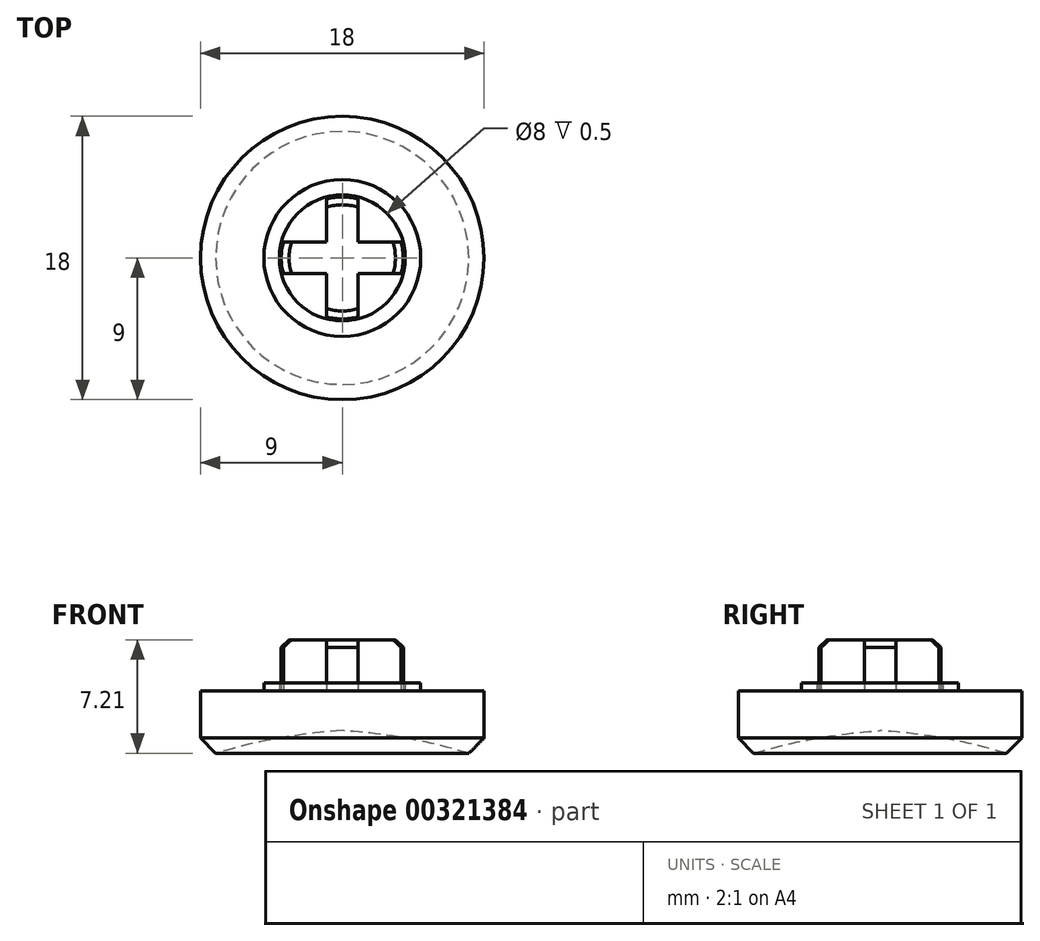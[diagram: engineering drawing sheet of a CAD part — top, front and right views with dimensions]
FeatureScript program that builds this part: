
annotation { "Feature Type Name" : "Feature", "Feature Type Description" : "" }
export const myFeature = defineFeature(function(context is Context, id is Id, definition is map)
    precondition{}
    {
        {
            var Q0;
            Q0=qCreatedBy(makeId("Top.planeOp"),FACE);
            var sketch = newSketch(context, id + "F0", { "sketchPlane" : qUnion([Q0])});
            skCircle(sketch, "E0", {"center": v(0, 0) * mm, "radius": 9 * mm});
            skLineSegment(sketch, "E1", {"start": v(-9.45, 0) * mm, "end": v(-9, 0) * mm});
            skLineSegment(sketch, "E2.left", {"start": v(-1, 3.74) * mm, "end": v(-1, 1) * mm});
            skLineSegment(sketch, "E2.right", {"start": v(1, 3.74) * mm, "end": v(1, 1) * mm});
            skLineSegment(sketch, "E3.bottom", {"start": v(-3.74, 1) * mm, "end": v(-1, 1) * mm});
            skLineSegment(sketch, "E3.top", {"start": v(-3.74, -1) * mm, "end": v(-1, -1) * mm});
            skCircle(sketch, "E4", {"center": v(0, 0) * mm, "radius": 3.88 * mm});
            skLineSegment(sketch, "E5.trimOffspring", {"start": v(1, 1) * mm, "end": v(3.74, 1) * mm});
            skLineSegment(sketch, "E6.trimOffspring", {"start": v(-1, -1) * mm, "end": v(-1, -3.74) * mm});
            skLineSegment(sketch, "E7.trimOffspring", {"start": v(1, -1) * mm, "end": v(1, -3.74) * mm});
            skLineSegment(sketch, "E8.trimOffspring", {"start": v(1, -1) * mm, "end": v(3.74, -1) * mm});
            skPoint(sketch, "E9.start.orphan", {"position": v(0, 9) * mm});
            skSolve(sketch);
        }
        {
            var Q0;
            Q0=qSketchRegion(id+"F0",true);
            extrude(context, id + "F1", {"entities" : qUnion([Q0]), "depth" : 4 * mm});
        }
        {
            var Q0;
            Q0=makeQuery(id+"F1.opExtrude","CAP_FACE",FACE,{"disambiguationData":[OSD([sQuery(id+"F0.wireOp",EDGE,"E0")])],"isStart":false});
            var sketch = newSketch(context, id + "F2", { "sketchPlane" : qUnion([Q0])});
            skCircle(sketch, "E10", {"center": v(0, 0) * mm, "radius": 4 * mm});
            skCircle(sketch, "E11", {"center": v(0, 0) * mm, "radius": 4.98 * mm});
            skSolve(sketch);
        }
        {
            var Q0;
            {var subQ5=sQuery(id+"F0.wireOp",EDGE,"E2.left");Q0=makeQuery(id+"F0.imprint","IMPRINT",FACE,{"disambiguationData":[TD([[makeQuery(id+"F0.imprint","IMPRINT",EDGE,{"derivedFrom":subQ5}),1.0]])]});}
            extrude(context, id + "F3", {"entities" : qUnion([Q0]), "operationType" : NewBodyOperationType.ADD, "depth" : 7.25 * mm});
        }
        {
            var Q0;
            {var subQ0=sQuery(id+"F0.wireOp",EDGE,"E2.left");Q0=makeQuery(id+"F0.imprint","IMPRINT",FACE,{"disambiguationData":[TD([[makeQuery(id+"F0.imprint","IMPRINT",EDGE,{"derivedFrom":subQ0}),-1.0]])]});}
            var Q1;
            {var subQ0=sQuery(id+"F0.wireOp",EDGE,"E2.right");Q1=makeQuery(id+"F0.imprint","IMPRINT",FACE,{"disambiguationData":[TD([[makeQuery(id+"F0.imprint","IMPRINT",EDGE,{"derivedFrom":subQ0}),1.0]])]});}
            var Q2;
            {var subQ0=sQuery(id+"F0.wireOp",EDGE,"E7.trimOffspring");Q2=makeQuery(id+"F0.imprint","IMPRINT",FACE,{"disambiguationData":[TD([[makeQuery(id+"F0.imprint","IMPRINT",EDGE,{"derivedFrom":subQ0}),1.0]])]});}
            var Q3;
            {var subQ0=sQuery(id+"F0.wireOp",EDGE,"E3.top");Q3=makeQuery(id+"F0.imprint","IMPRINT",FACE,{"disambiguationData":[TD([[makeQuery(id+"F0.imprint","IMPRINT",EDGE,{"derivedFrom":subQ0}),-1.0]])]});}
            extrude(context, id + "F4", {"entities" : qUnion([Q0, Q1, Q2, Q3]), "operationType" : NewBodyOperationType.ADD, "depth" : 4 * mm});
        }
        {
            var Q0;
            {var subQ0=sQuery(id+"F0.wireOp",EDGE,"E4");Q0=makeQuery(id+"F3.opExtrude","CAP_EDGE",EDGE,{"disambiguationData":[OSD([subQ0]),TDD([makeQuery(id+"F0.imprint","IMPRINT",EDGE,{"disambiguationData":[TD([[makeQuery(id+"F0.imprint","INTERSECT",VERTEX,{"derivedFrom":[sQuery(id+"F0.wireOp",EDGE,"E3.bottom"),subQ0]}),-1.0]])],"derivedFrom":subQ0})])],"isStart":false});}
            var Q1;
            {var subQ0=sQuery(id+"F0.wireOp",EDGE,"E4");Q1=makeQuery(id+"F3.opExtrude","CAP_EDGE",EDGE,{"disambiguationData":[OSD([subQ0]),TDD([makeQuery(id+"F0.imprint","IMPRINT",EDGE,{"disambiguationData":[TD([[makeQuery(id+"F0.imprint","INTERSECT",VERTEX,{"derivedFrom":[sQuery(id+"F0.wireOp",EDGE,"E2.left"),subQ0]}),1.0]])],"derivedFrom":subQ0})])],"isStart":false});}
            var Q2;
            {var subQ0=sQuery(id+"F0.wireOp",EDGE,"E4");Q2=makeQuery(id+"F3.opExtrude","CAP_EDGE",EDGE,{"disambiguationData":[OSD([subQ0]),TDD([makeQuery(id+"F0.imprint","IMPRINT",EDGE,{"disambiguationData":[TD([[makeQuery(id+"F0.imprint","INTERSECT",VERTEX,{"derivedFrom":[subQ0,sQuery(id+"F0.wireOp",EDGE,"E5.trimOffspring")]}),1.0]])],"derivedFrom":subQ0})])],"isStart":false});}
            var Q3;
            {var subQ0=sQuery(id+"F0.wireOp",EDGE,"E4");Q3=makeQuery(id+"F3.opExtrude","CAP_EDGE",EDGE,{"disambiguationData":[OSD([subQ0]),TDD([makeQuery(id+"F0.imprint","IMPRINT",EDGE,{"disambiguationData":[TD([[makeQuery(id+"F0.imprint","INTERSECT",VERTEX,{"derivedFrom":[subQ0,sQuery(id+"F0.wireOp",EDGE,"E6.trimOffspring")]}),-1.0]])],"derivedFrom":subQ0})])],"isStart":false});}
            chamfer(context, id + "F5", {"entities" : qUnion([Q0, Q1, Q2, Q3]), "width" : 0.5 * mm, "tangentPropagation" : true});
        }
        {
            var Q0;
            {var subQ0=sQuery(id+"F0.wireOp",EDGE,"E8.trimOffspring");var subQ1=sQuery(id+"F0.wireOp",EDGE,"E7.trimOffspring");var subQ2=sQuery(id+"F0.wireOp",EDGE,"E4");var subQ3=sQuery(id+"F0.wireOp",EDGE,"E6.trimOffspring");var subQ4=sQuery(id+"F0.wireOp",EDGE,"E3.top");var subQ5=sQuery(id+"F0.wireOp",EDGE,"E5.trimOffspring");var subQ6=sQuery(id+"F0.wireOp",EDGE,"E2.right");var subQ7=sQuery(id+"F0.wireOp",EDGE,"E3.bottom");var subQ8=sQuery(id+"F0.wireOp",EDGE,"E2.left");Q0=makeQuery(id+"F4.boolean.opBoolean","MERGE",FACE,{"derivedFrom":[makeQuery(id+"F3.boolean.opBoolean","MERGE",FACE,{"derivedFrom":[makeQuery(id+"F1.opExtrude","CAP_FACE",FACE,{"disambiguationData":[OSD([sQuery(id+"F0.wireOp",EDGE,"E0"),subQ2])],"isStart":true}),makeQuery(id+"F3.opExtrude","CAP_FACE",FACE,{"disambiguationData":[OSD([subQ8,subQ6,subQ7,subQ4,subQ2,subQ5,subQ3,subQ1,subQ0])],"isStart":true})]}),makeQuery(id+"F4.opExtrude","CAP_FACE",FACE,{"disambiguationData":[OSD([subQ8,subQ7,subQ2])],"isStart":true}),makeQuery(id+"F4.opExtrude","CAP_FACE",FACE,{"disambiguationData":[OSD([subQ6,subQ2,subQ5])],"isStart":true}),makeQuery(id+"F4.opExtrude","CAP_FACE",FACE,{"disambiguationData":[OSD([subQ4,subQ2,subQ3])],"isStart":true}),makeQuery(id+"F4.opExtrude","CAP_FACE",FACE,{"disambiguationData":[OSD([subQ2,subQ1,subQ0])],"isStart":true})]});}
            chamfer(context, id + "F6", {"entities" : qUnion([Q0]), "width" : 1 * mm, "tangentPropagation" : true});
        }
        {
            var Q0;
            Q0=qCreatedBy(makeId("Right.planeOp"),FACE);
            var sketch = newSketch(context, id + "F7", { "sketchPlane" : qUnion([Q0])});
            skLineSegment(sketch, "E12", {"start": v(0, 0) * mm, "end": v(0, 1.48) * mm});
            skLineSegment(sketch, "E13", {"start": v(0, 0) * mm, "end": v(8.16, 0) * mm});
            skArc(sketch, "E14", {"start": v(8.16, 0) * mm, "mid": v(4.12, 0.98) * mm, "end": v(0, 1.48) * mm});
            skLineSegment(sketch, "E15", {"start": v(0, -0.97) * mm, "end": v(0, 1.81) * mm, "construction": true});
            skSolve(sketch);
        }
        {
            var Q0;
            Q0=makeQuery(id+"F7.imprint","IMPRINT",FACE,{"disambiguationData":[TD([[makeQuery(id+"F7.imprint","IMPRINT",EDGE,{"derivedFrom":sQuery(id+"F7.wireOp",EDGE,"E12")}),-1.0]])]});
            var Q1;
            Q1=sQuery(id+"F7.wireOp",EDGE,"E15");
            revolve(context, id + "F8", {"operationType" : NewBodyOperationType.REMOVE, "entities" : qUnion([Q0]), "axis" : qUnion([Q1]), "revolveType" : RevolveType.FULL, "oppositeDirection" : true});
        }
        {
            var Q0;
            Q0=qSketchRegion(id+"F2",true);
            extrude(context, id + "F9", {"entities" : qUnion([Q0]), "operationType" : NewBodyOperationType.ADD, "depth" : .5 * mm});
        }
    });
